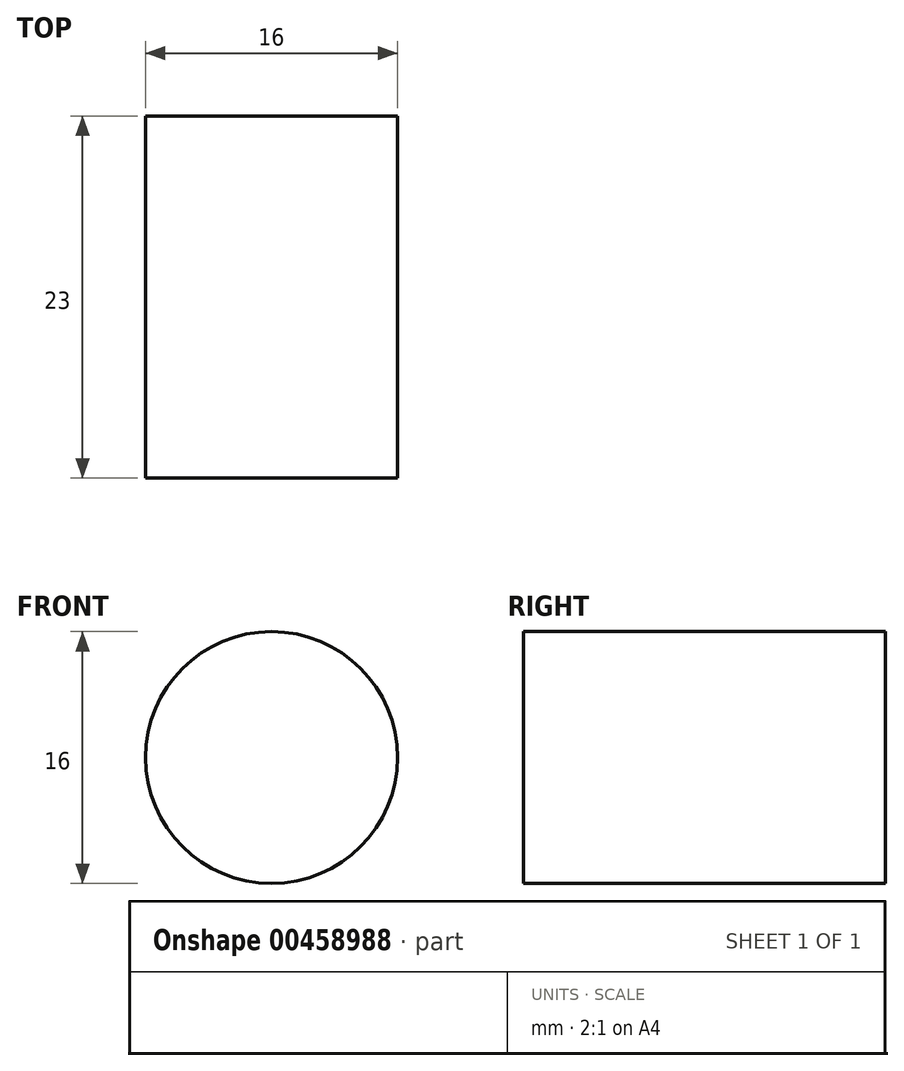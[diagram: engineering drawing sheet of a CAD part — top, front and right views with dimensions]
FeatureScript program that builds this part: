
annotation { "Feature Type Name" : "Feature", "Feature Type Description" : "" }
export const myFeature = defineFeature(function(context is Context, id is Id, definition is map)
    precondition{}
    {
        {
            var Q0;
            Q0=qCreatedBy(makeId("Front.planeOp"),FACE);
            var sketch = newSketch(context, id + "F0", { "sketchPlane" : qUnion([Q0])});
            skCircle(sketch, "E0", {"center": v(0, 0) * mm, "radius": 8 * mm});
            skSolve(sketch);
        }
        {
            var Q0;
            Q0 = qSketchRegion(id + "F0", true);
            extrude(context, id + "F1", {"entities" : qUnion([Q0]), "depth" : 23 * mm});
        }
    });
